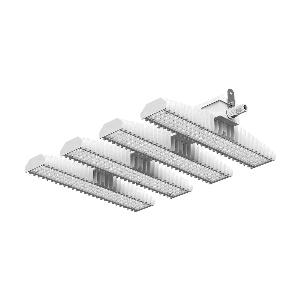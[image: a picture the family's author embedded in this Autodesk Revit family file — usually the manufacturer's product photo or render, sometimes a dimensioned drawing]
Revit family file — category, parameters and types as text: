
# Revit family: 3f_filippi_-_3f_lem_ampio_3f_filippi_-_58902_-_3f_lem_4_led_200_dali_cr_ampio
name_source: partatom
category: Lighting Fixtures
units: mm (PartAtom-declared; Revit-internal decimal feet)

## family parameters
Cut with Voids When Loaded = No
Host = Face
Light Source = No
Part Type = Normal
Room Calculation Point = No
Round Connector Dimension = Use Diameter
Shared = No

## types (1)
- 3F Filippi - 3F LEM Ampio (1 x LED, 33978 lm, 218 W, 4000 K)
    Apparent Load = 218 VA
    Approval mark = CE
    CIE Flux Codes = 60 92 99 100 100
    Color Rendering = 80
    Color Temperature = 4000 K
    Control Gear = Electronic transformer
    Default Elevation = 1800 mm
    Description = Industrial luminaire with high light output and high luminous efficiency designed with the most innovative technologies for environments with temperature up to 55°C.

ILLUMINOTECHNICAL
Luminous efficiency 100% (DLOR 100%, ULOR 0%).
Initial luminous flux of the luminaire 33978 lm.
Direct symmetric wide distribution: the illuminated area has a rectangular shape.
Installation Interdistance Transv.D = 1.58 x hu - Long.D = 1.45 x hu.
Tabular UGR (CIE 117 - 4H-8H; S=0.25H; 70/50/20): RUG 23.2 - 24.2.
Beam angle: 93° - 99°.
Luminous efficacy 156 lm/W.
Lifetime (L93/B10): 30000 h. (tq+25°C)
Lifetime (L90/B10): 50000 h. (tq+25°C)
Lifetime (L85/B10): 80000 h. (tq+25°C)
Lifetime (L80/B10): 100000 h. (tq+25°C)
Lifetime (L85/B10): 50000 h. (tq+55°C)
Sudden decreased luminous flux after 50000 hours: 0% (C0).
Photobiological safety in compliance with IEC/TR 62778: RG0 risk exempt, (IEC 62471).
In compliance with IEC/EN 62722-2-1 - IEC/EN 62717 standards.

SOURCE
4 Mid-Power linear LED modules 50W/840.
Energy efficiency class (UE 2019/2020 - UE 2019/2015): C.
CIE 13.3 Colour rendering index: CRI >80 (R9 <50%).
IES TM-30 Fidelity Index: Rf = 84 Rg = 95.
CCT nominal colour temperature 4000 K.
Colour initial tolerance (MacAdam): SDCM 3.

MECHANICAL
Passive modular heatsinks in die-casted aluminium, painted in white colour.
To optimize the thermal management of the LED module, the heatsinks are oversized and provided with self-cleaning of cooling fins.
Wiring body in aluminium and galvanised steel anchored solidly to the sinks and thermally separated.
3F Lens lenses with high luminous efficiency, transparent methacrylate (PMMA), fixed to the LED modules.
Fixing brackets in stainless steel.
Luminaire with limited surface temperature. - D - (EN 60598-2-24)
Dimensions: 757x542 mm, height 129 mm. Weight 17.445 kg.
IP65 protection degree.
Mechanical strength to impacts IK06 (1 joule).
Glow-wire test resistance 650°C.

ELECTRICAL
Halogen Free DALI-2 DATI (Parts 251, 252, 253), PUSH-DIM, electronic wiring 230V-50/60Hz, power factor 0.97 at full load, THD <25%, constant output current, class I, 2 driver, 2 DALI addresses.
Power of the luminaire 218 W.
ENEC - CE.
Flicker: <4%.
Luminaire compliant with EN 60598-2-22 for power supply from a centralised emergency system CPSS (Central Power Supply System), not incorporated in the luminaire - high risk areas excluded. The default power and flux are 100% in AC and 15% in DC.
Ambient temperature from -30°C to +55°C.
Temperature class T6 max 85°C.
Quick connection via M25 5P connector with 9-13 mm tightening range.
Power unit positioned on a separate compartment by the LED module to ensure optimum temperatures of cabling components, to be inspectable and maintainable.
Relative humidity UR: <85%.

INSTALLATION
Ceiling / Suspended / Wall.
All accessories dedicated to this product are available on the Catalog and on our website www.3F-Filippi.com.

APPLICATIONS
In commercial environments, exhibition and industrial areas, stores, open areas.
Applications with high ambient temperature up to 55°C.
Environments in which it is necessary a total protection against falling fragments (eg environments with foodstuffs or machines with moving parts or with extreme temperature changes), use luminaires with polycarbonate lenses.

LIGHT MANAGEMENT
Recommended minimum setting: 10%.
The luminaire, equipped with (DALI-2 DATI) driver, can be controlled manually with 3F Easy Dim technology or automatically/manually with wired or wireless DALI/D2D control systems.
The D2D driver guarantees interoperability with other devices with the same certification by making the following information available:
Device Data (Part 251), Energy Report (Part 252), Diagnosis & Maintenance (Part 253).
In electrical systems without a regulation system (manual or automatic) and DALI bus, a suitable jumper must be made on the DA-DA terminals of the appliance.

WARNING
Fixture not suitable for cold stores with an ambient temperature <0°C and/or relative humidity >85%.
Luminaire designed for disposal/recycling at end-of-life.
Replaceable (LED only) light source by a professional. Replaceable control gear by a professional.
    Height = 129 mm
    Lamp = 1 x LED
    Lamp Light Flux = 33978 lm
    Lamp Power = 218 W
    Lamp count = 1
    Length = 757 mm
    Lifetime = 50000 h
    Luminous efficacy = 156 lm/W
    Manufacturer = 3F Filippi
    ModVariant = No
    Model = 3F Filippi - 58902 - 3F LEM 4 LED 200 DALI CR AMPIO
    Mounting Place = Ceiling
    Mounting Type = Pendant
    Number of Poles = 1
    OnlyDefault = Yes
    Power Factor = 1
    Product Name = 3F Filippi - 3F LEM Ampio
    Product group = pendant luminaire
    ProductGroupID = 9
    Protection Class = Protection class I
    Protection Degree = IP 65
    RLX_Detail_Level = 1
    RLX_Emergency_Light_Flux = 0 lm
    RLX_Emergency_Type = 0
    RLX_Emergency_Type_DB = No
    RlxData = <blob elided: 118337 chars, md5=9d39885a>
    Socket = socket
    Standby Power = 0 W
    System Light Flux = 33978 lm
    System Power = 218 W
    Type Comments = Product without accessories
    Type Image = 3f_filippi_-_lem_4.jpg
    URL = http://relux.com
    VarID = ---
    Voltage = 0 V
    Weight = 0.00 kg
    Width = 542 mm

## geometry (parser evidence)
native form markers: Blend x4, Sweep x15
no freeform markers — native parametric forms only
